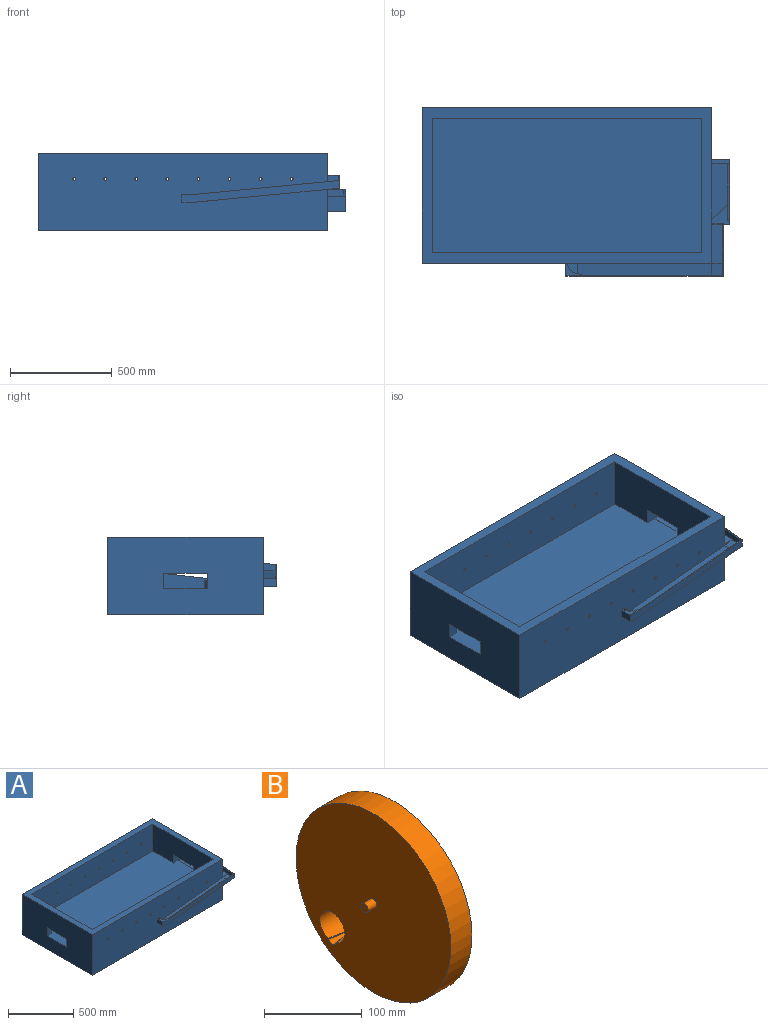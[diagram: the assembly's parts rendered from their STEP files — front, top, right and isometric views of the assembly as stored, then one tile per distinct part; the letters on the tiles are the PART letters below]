
ASSEMBLY  parts=2 mates=1
PART A: 94 faces, bbox 1511.3x825.8x381 mm
  f0: plane 1320.8x254mm, normal (0,1,0), area 333168.8mm2, adj f2,f4,f14,f18,f19,f20,f27,f28
  f1: plane 1473.2x381mm, normal (0,-1,0), area 536125.4mm2, adj f2,f3,f4,f7,f13,f14,f16,f27
  f2: cylinder r=16.51mm len=50.8mm, axis (0,-1,0), area 1317.4mm2, adj f0,f1,f91,f93
  f3: plane 660.4x63.7mm, normal (-0.1,0,1), area 38881.2mm2, adj f1,f4,f72,f78,f88
  f4: plane 102.28x50.8mm, normal (0,0,1), area 3488.9mm2, adj f0,f1,f3,f88,f89,f90,f91,f92
  f5: plane 195.26x0.16mm, normal (1,0,0), area 15.3mm2, adj f6,f71,f74
  f6: plane 195.26x50.8mm, normal (0,0,-1), area 9919.3mm2, adj f5,f7,f62,f67
  f7: plane 762x381mm, normal (1,0,0), area 256988.3mm2, adj f1,f6,f10,f11,f12,f14,f15,f16
  f8: plane 27.51x15.9mm, normal (1,0,0), area 121.2mm2, adj f60,f64,f65
  f9: plane 228.6x228.03mm, normal (-1,0,0), area 36455.4mm2, adj f10,f11,f12,f43,f50,f57,f58,f59
  f10: plane 7.62x0.17mm, normal (0,0.02,-1), area 1.3mm2, adj f7,f9,f11,f59
  f11: plane 7.62x0.54mm, normal (0,-0.95,0.3), area 4.3mm2, adj f7,f9,f10,f58
  f12: cylinder r=20.2mm len=40.41mm, axis (1,0,0), area 527mm2, adj f7,f9,f55,f57,f59
  f13: plane 762x381mm, normal (-1,0,0), area 274112.4mm2, adj f1,f14,f15,f16,f20,f21,f22,f23
  f14: plane 1422.4x762mm, normal (0,0,1), area 211612.5mm2, adj f0,f1,f7,f13,f15,f17,f18,f19
  f15: plane 1422.4x381mm, normal (0,1,0), area 540651.8mm2, adj f7,f13,f14,f16,f35,f36,f37,f38
  f16: plane 1422.4x762mm, normal (0,0,-1), area 1083868.8mm2, adj f1,f7,f13,f15
  f17: plane 1320.8x254mm, normal (0,-1,0), area 334200.6mm2, adj f14,f18,f19,f20,f35,f36,f37,f38
  f18: plane 660.4x254mm, normal (1,0,0), area 151532mm2, adj f0,f14,f17,f20,f21,f22,f23
  f19: plane 660.4x254mm, normal (-1,0,0), area 151450.9mm2, adj f0,f14,f17,f20,f24,f25,f26,f49
  f20: plane 1422.4x660.4mm, normal (0,0,1), area 893869.2mm2, adj f0,f7,f13,f17,f18,f19,f21,f22
  f21: plane 76.2x50.8mm, normal (0,1,0), area 3871mm2, adj f13,f18,f20,f23
  f22: plane 76.2x50.8mm, normal (0,-1,0), area 3871mm2, adj f13,f18,f20,f23
  f23: plane 212.73x50.8mm, normal (0,0,-1), area 10806.4mm2, adj f13,f18,f21,f22
  f24: plane 76.2x50.8mm, normal (0,1,0), area 3871mm2, adj f7,f19,f20,f26
  f25: plane 127x76.2mm, normal (0,-1,0), area 9677.4mm2, adj f19,f20,f26,f43,f48,f54
  f26: plane 212.73x50.8mm, normal (0,0,-1), area 10806.4mm2, adj f7,f19,f24,f25
  f27: cylinder r=7.14mm len=50.8mm, axis (0,-1,0), area 2280.2mm2, adj f0,f1
  f28: cylinder r=7.14mm len=50.8mm, axis (0,-1,0), area 2280.2mm2, adj f0,f1
  f29: cylinder r=7.14mm len=50.8mm, axis (0,-1,0), area 2280.2mm2, adj f0,f1
  f30: cylinder r=7.14mm len=50.8mm, axis (0,-1,0), area 2280.2mm2, adj f0,f1
  f31: cylinder r=7.14mm len=50.8mm, axis (0,-1,0), area 2280.2mm2, adj f0,f1
  f32: cylinder r=7.14mm len=50.8mm, axis (0,-1,0), area 2280.2mm2, adj f0,f1
  f33: cylinder r=7.14mm len=50.8mm, axis (0,-1,0), area 2280.2mm2, adj f0,f1
  f34: cylinder r=7.14mm len=50.8mm, axis (0,-1,0), area 2280.2mm2, adj f0,f1
  f35: cylinder r=7.14mm len=50.8mm, axis (0,-1,0), area 2280.2mm2, adj f15,f17
  f36: cylinder r=7.14mm len=50.8mm, axis (0,-1,0), area 2280.2mm2, adj f15,f17
  f37: cylinder r=7.14mm len=50.8mm, axis (0,-1,0), area 2280.2mm2, adj f15,f17
  f38: cylinder r=7.14mm len=50.8mm, axis (0,-1,0), area 2280.2mm2, adj f15,f17
  f39: cylinder r=7.14mm len=50.8mm, axis (0,-1,0), area 2280.2mm2, adj f15,f17
  f40: cylinder r=7.14mm len=50.8mm, axis (0,-1,0), area 2280.2mm2, adj f15,f17
  f41: cylinder r=7.14mm len=50.8mm, axis (0,-1,0), area 2280.2mm2, adj f15,f17
  f42: cylinder r=7.14mm len=50.8mm, axis (0,-1,0), area 2280.2mm2, adj f15,f17
  f43: plane 270.35x83.82mm, normal (0,-0.05,1), area 18316.8mm2, adj f7,f9,f25,f54,f56,f57,f58
  f44: plane 95.2x88.9mm, normal (0,0,1), area 4907.5mm2, adj f7,f45,f52,f53,f54,f56
  f45: plane 88.9x76.2mm, normal (0,-1,0), area 6774.2mm2, adj f7,f44,f46,f53
  f46: plane 317.5x88.9mm, normal (0,0.05,-1), area 28255.4mm2, adj f7,f45,f47,f53
  f47: plane 94.66x88.9mm, normal (0,1,0), area 8414.9mm2, adj f7,f46,f48,f53
  f48: plane 88.9x20.32mm, normal (0,0,1), area 1806.4mm2, adj f7,f25,f47,f52,f53
  f49: cylinder r=5.08mm len=12.7mm, axis (1,0,0), area 405.4mm2, adj f19,f51
  f50: cylinder r=114.3mm len=228.6mm, axis (-1,0,0), area 21483.4mm2, adj f9,f51,f60,f61
  f51: plane 228.6x228.6mm, normal (1,0,0), area 40962.2mm2, adj f49,f50
  f52: plane 276.86x33.02mm, normal (0,-0.12,0.99), area 3541mm2, adj f44,f48,f53,f54
  f53: plane 317.5x109.22mm, normal (1,0,0), area 27123.4mm2, adj f44,f45,f46,f47,f48,f52
  f54: plane 276.86x85.47mm, normal (-1,0,0), area 14228.2mm2, adj f25,f43,f44,f52,f56
  f55: plane 11.22x0.79mm, normal (-1,0,0), area 6mm2, adj f12,f56
  f56: plane 76.2x68.36mm, normal (-0.67,0.74,0), area 5529.5mm2, adj f7,f43,f44,f54,f55,f57
  f57: plane 15.51x7.62mm, normal (0,1,0), area 118.2mm2, adj f9,f12,f43,f56
  f58: plane 16.16x7.62mm, normal (0,-1,0), area 123.2mm2, adj f7,f9,f11,f43
  f59: plane 7.62x2.6mm, normal (0,-1,0), area 19.8mm2, adj f7,f9,f10,f12
  f60: cylinder r=31.75mm len=63.5mm, axis (1,0,0), area 1935mm2, adj f7,f8,f9,f50,f61,f66
  f61: plane 22.82x2.12mm, normal (1,0,0), area 23.8mm2, adj f50,f60
  f62: plane 63.5x55.88mm, normal (0,1,0), area 3548.4mm2, adj f6,f7,f63,f74,f76
  f63: plane 55.88x7.62mm, normal (0,0,1), area 425.8mm2, adj f7,f62,f64,f75,f76
  f64: plane 50.8x44.26mm, normal (0,-1,0), area 2248.5mm2, adj f7,f8,f63,f65,f73
  f65: plane 187.64x50.8mm, normal (0,-0.05,1), area 9542.8mm2, adj f1,f7,f8,f64,f66,f73
  f66: plane 29.04x4.24mm, normal (-1,0,0), area 69.1mm2, adj f60,f65
  f67: plane 50.8x4.9mm, normal (0,1,0), area 124.5mm2, adj f6,f7,f68
  f68: plane 711.2x68.6mm, normal (0.1,0,-1), area 45597.7mm2, adj f1,f67,f69,f70,f79,f83
  f69: plane 58.74x0.2mm, normal (1,0,0), area 10.6mm2, adj f68,f71,f74,f77
  f70: plane 63.82x50.8mm, normal (0,0,-1), area 3241.9mm2, adj f1,f68,f83,f84
  f71: plane 0.16x0mm, normal (0,1,0), area 0mm2, adj f5,f69,f74
  f72: plane 58.74x50.8mm, normal (-0.14,0,0.99), area 3015.5mm2, adj f1,f3,f73,f78
  f73: plane 246.38x55.88mm, normal (-1,0,0), area 9313.7mm2, adj f1,f64,f65,f72,f75,f78
  f74: plane 254x5.08mm, normal (0,0,-1), area 1290.3mm2, adj f5,f62,f69,f71,f76,f77
  f75: plane 246.38x25.2mm, normal (0,-0.1,0.99), area 1258.1mm2, adj f63,f73,f76,f80
  f76: plane 259.08x63.5mm, normal (1,0,0), area 13193.8mm2, adj f62,f63,f74,f75,f77,f79,f80,f83
  f77: plane 5.08x0.2mm, normal (0,1,0), area 1mm2, adj f69,f74,f76,f79
  f78: plane 710.96x99.45mm, normal (0,1,0), area 22764.9mm2, adj f3,f72,f73,f81,f85,f88
  f79: plane 5.08x5.08mm, normal (0,0,-1), area 25.8mm2, adj f68,f76,f77,f83
  f80: plane 5.08x5.08mm, normal (0,0,1), area 25.8mm2, adj f75,f76,f81,f83
  f81: plane 711.2x68.6mm, normal (-0.1,0,1), area 3629.7mm2, adj f78,f80,f82,f83,f87
  f82: plane 50.8x5.08mm, normal (0,0,1), area 258.1mm2, adj f81,f83,f85,f87
  f83: plane 772.16x106.91mm, normal (0,-1,0), area 29576.3mm2, adj f68,f70,f76,f79,f80,f81,f82,f84
  f84: plane 63.82x5.08mm, normal (0,0,-1), area 324.2mm2, adj f1,f70,f83,f86
  f85: plane 80.31x63.82mm, normal (0,0,1), area 1585.2mm2, adj f1,f78,f82,f83,f86,f87,f88,f89
  f86: plane 63.82x38.3mm, normal (-1,0,0), area 2444.4mm2, adj f1,f83,f84,f85
  f87: plane 51.04x0.02mm, normal (0,-1,0), area 0.6mm2, adj f81,f82,f85
  f88: plane 44.77x33.22mm, normal (0.28,0.96,0), area 1521.8mm2, adj f3,f4,f78,f85,f89
  f89: cylinder r=18.46mm len=33.22mm, axis (0,0,1), area 638.4mm2, adj f4,f85,f88,f90
  f90: plane 34.36x33.22mm, normal (0.91,0.42,0), area 1256.6mm2, adj f1,f4,f85,f89,f92
  f91: plane 50.8x16.51mm, normal (-1,0,0), area 838.7mm2, adj f0,f1,f2,f4
  f92: plane 50.8x33.02mm, normal (1,0,0), area 1677.4mm2, adj f0,f4,f90,f93
  f93: plane 50.8x16.51mm, normal (0,0,-1), area 838.7mm2, adj f0,f1,f2,f92
PART B: 15 faces, bbox 43.6x223.9x223.9 mm
  f0: cylinder r=17.78mm len=30.48mm, axis (1,0,0), area 1069.2mm2, adj f1,f4,f7,f10,f11
  f1: plane 223.52x223.52mm, normal (1,0,0), area 38193.7mm2, adj f0,f2,f6,f10,f11,f12,f13
  f2: cylinder r=17.78mm len=35.53mm, axis (1,0,0), area 1923.4mm2, adj f1,f5,f7,f10,f12
  f3: plane 22.38x6.35mm, normal (0,0.71,-0.71), area 26mm2, adj f4,f5,f7,f10
  f4: plane 22.5x2.92mm, normal (0.17,0.7,0.7), area 4mm2, adj f0,f3,f7,f10
  f5: plane 22.5x2.92mm, normal (0.17,-0.7,-0.7), area 4mm2, adj f2,f3,f7,f10
  f6: cylinder r=111.76mm len=223.52mm, axis (-1,0,0), area 21403.3mm2, adj f1,f7
  f7: plane 223.52x223.52mm, normal (-1,0,0), area 38131.4mm2, adj f0,f2,f3,f4,f5,f6,f8,f11
  f8: cylinder r=5.08mm len=12.7mm, axis (1,0,0), area 405.4mm2, adj f7,f9
  f9: plane 10.16x10.16mm, normal (-1,0,0), area 81.1mm2, adj f8
  f10: cone r=0mm half-angle=11.8deg, axis (1,0,0), area 247.1mm2, adj f0,f1,f2,f3,f4,f5
  f11: plane 30.89x5.11mm, normal (-0.15,0.99,0), area 18.8mm2, adj f0,f1,f7,f13
  f12: plane 30.87x4.96mm, normal (-0.15,-0.99,0), area 18.1mm2, adj f1,f2,f7,f13
  f13: plane 30.48x11.37mm, normal (0,0,1), area 30.2mm2, adj f1,f7,f11,f12,f14
  f14: cone r=0mm half-angle=7.7deg, axis (-1,0,0), area 205.7mm2, adj f7,f13
PLACE A t=(231.93,207.94,130.01)mm
PLACE B t=(1617.23,363.83,300.19)mm
MATE cylindrical B.f6 <-> A.f49  axis (-1,0,0) through (1617.23,363.83,300.19)mm
